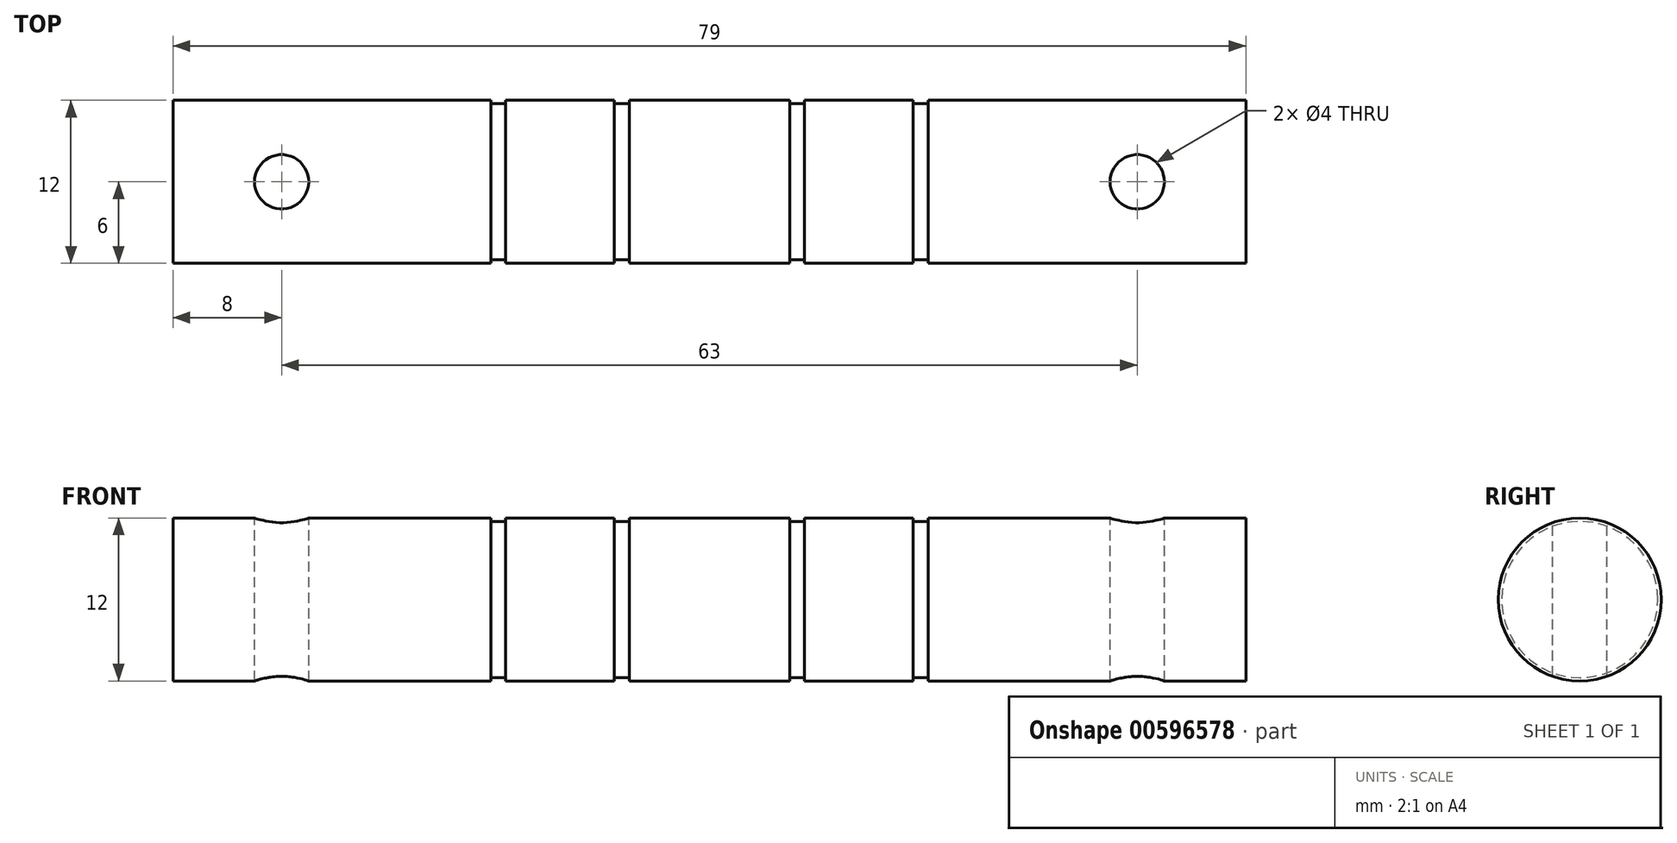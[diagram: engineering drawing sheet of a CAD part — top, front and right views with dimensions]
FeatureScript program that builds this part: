
annotation { "Feature Type Name" : "Feature", "Feature Type Description" : "" }
export const myFeature = defineFeature(function(context is Context, id is Id, definition is map)
    precondition{}
    {
        {
            var Q0;
            Q0=qCreatedBy(makeId("Front.planeOp"),FACE);
            var sketch = newSketch(context, id + "F0", { "sketchPlane" : qUnion([Q0])});
            skLineSegment(sketch, "E0", {"start": v(0, 0) * mm, "end": v(79, 0) * mm});
            skLineSegment(sketch, "E1", {"start": v(0, 0) * mm, "end": v(0, 6) * mm});
            skLineSegment(sketch, "E2", {"start": v(0, 6) * mm, "end": v(23.4, 6) * mm});
            skLineSegment(sketch, "E3", {"start": v(79, 6) * mm, "end": v(79, 0) * mm});
            skLineSegment(sketch, "E4.0", {"start": v(24.5, 5.75) * mm, "end": v(24.5, 6) * mm});
            skLineSegment(sketch, "E5.0", {"start": v(23.4, 5.75) * mm, "end": v(23.4, 6) * mm});
            skLineSegment(sketch, "E6.0", {"start": v(23.4, 5.75) * mm, "end": v(24.5, 5.75) * mm});
            skLineSegment(sketch, "E7.trimOffspring", {"start": v(24.5, 6) * mm, "end": v(32.5, 6) * mm});
            skLineSegment(sketch, "E8.0", {"start": v(32.5, 5.75) * mm, "end": v(32.5, 6) * mm});
            skLineSegment(sketch, "E9.0", {"start": v(33.6, 5.75) * mm, "end": v(33.6, 6) * mm});
            skLineSegment(sketch, "E10.trimOffspring", {"start": v(33.6, 6) * mm, "end": v(45.4, 6) * mm});
            skLineSegment(sketch, "E11.trimOffspring", {"start": v(32.5, 5.75) * mm, "end": v(33.6, 5.75) * mm});
            skLineSegment(sketch, "E12.0", {"start": v(45.4, 5.75) * mm, "end": v(45.4, 6) * mm});
            skLineSegment(sketch, "E13.trimOffspring", {"start": v(45.4, 5.75) * mm, "end": v(46.5, 5.75) * mm});
            skLineSegment(sketch, "E14.0", {"start": v(46.5, 5.75) * mm, "end": v(46.5, 6) * mm});
            skLineSegment(sketch, "E15.trimOffspring", {"start": v(46.5, 6) * mm, "end": v(54.5, 6) * mm});
            skLineSegment(sketch, "E16.0", {"start": v(54.5, 5.75) * mm, "end": v(54.5, 6) * mm});
            skLineSegment(sketch, "E17.trimOffspring", {"start": v(54.5, 5.75) * mm, "end": v(55.6, 5.75) * mm});
            skLineSegment(sketch, "E18.0", {"start": v(55.6, 5.75) * mm, "end": v(55.6, 6) * mm});
            skLineSegment(sketch, "E19.trimOffspring", {"start": v(55.6, 6) * mm, "end": v(79, 6) * mm});
            skSolve(sketch);
        }
        {
            var Q0;
            Q0=makeQuery(id+"F0.imprint","IMPRINT",FACE,{"disambiguationData":[TD([[makeQuery(id+"F0.imprint","IMPRINT",EDGE,{"derivedFrom":sQuery(id+"F0.wireOp",EDGE,"E0")}),1.0]])]});
            var Q1;
            Q1=sQuery(id+"F0.wireOp",EDGE,"E0");
            revolve(context, id + "F1", {"entities" : qUnion([Q0]), "axis" : qUnion([Q1]), "revolveType" : RevolveType.FULL});
        }
        {
            var Q0;
            Q0=qCreatedBy(makeId("Top.planeOp"),FACE);
            var sketch = newSketch(context, id + "F2", { "sketchPlane" : qUnion([Q0])});
            skCircle(sketch, "E20", {"center": v(71, 0) * mm, "radius": 2 * mm});
            skCircle(sketch, "E21", {"center": v(8, 0) * mm, "radius": 2 * mm});
            skSolve(sketch);
        }
        {
            var Q0;
            Q0 = qSketchRegion(id + "F2", true);
            extrude(context, id + "F3", {"entities" : qUnion([Q0]), "operationType" : NewBodyOperationType.REMOVE, "endBound" : BoundingType.THROUGH_ALL, "oppositeDirection" : true, "depth" : 25 * mm, "offsetDistance" : 25 * mm, "hasSecondDirection" : true, "secondDirectionBound" : SecondDirectionBoundingType.THROUGH_ALL, "secondDirectionOppositeDirection" : false, "secondDirectionDepth" : 25 * mm});
        }
    });
